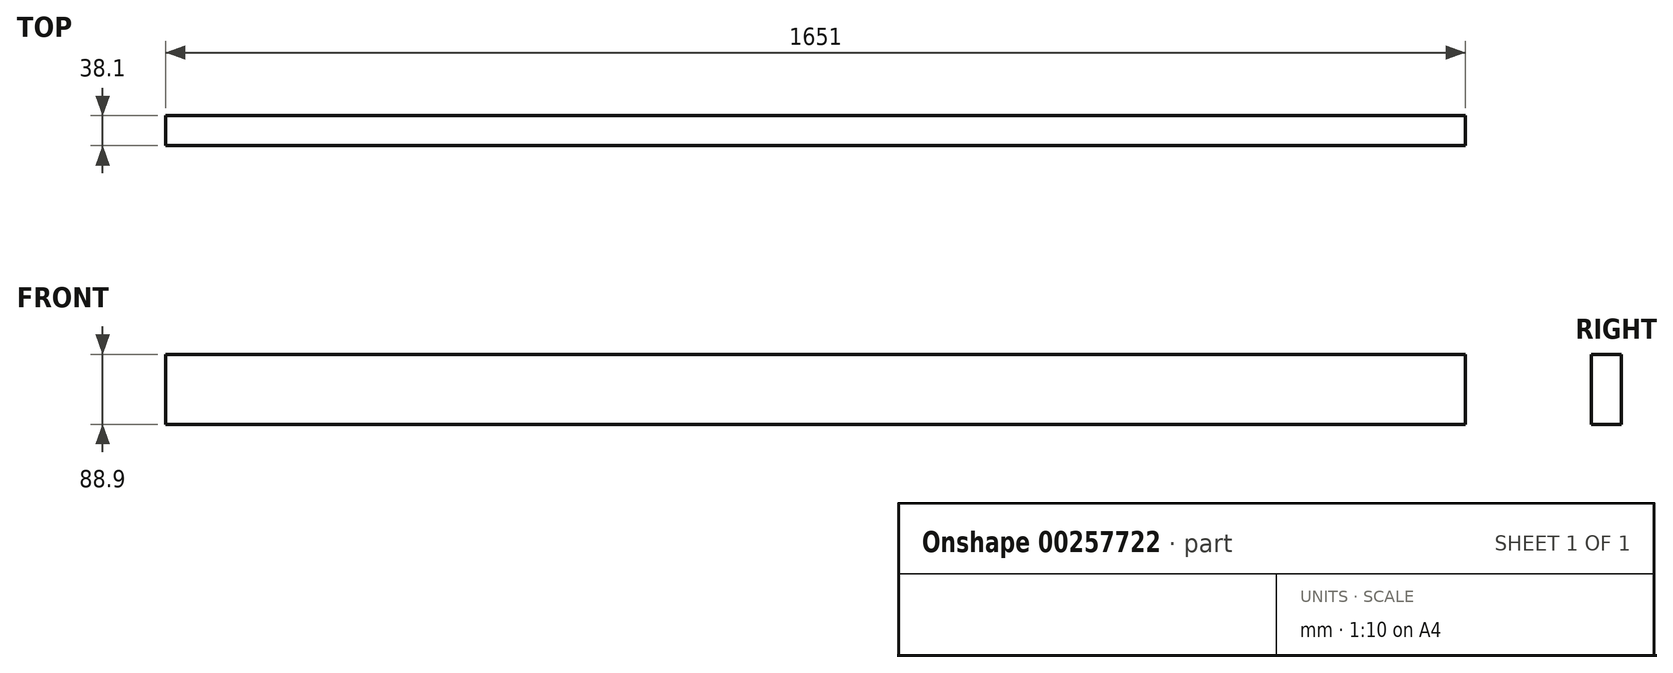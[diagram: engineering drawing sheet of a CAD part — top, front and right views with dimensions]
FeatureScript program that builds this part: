
annotation { "Feature Type Name" : "Feature", "Feature Type Description" : "" }
export const myFeature = defineFeature(function(context is Context, id is Id, definition is map)
    precondition{}
    {
        {
            var Q0;
            Q0=qCreatedBy(makeId("Top.planeOp"),FACE);
            var sketch = newSketch(context, id + "F0", { "sketchPlane" : qUnion([Q0])});
            skLineSegment(sketch, "E0.bottom", {"start": v(-825.5, 19.05) * mm, "end": v(825.5, 19.05) * mm});
            skLineSegment(sketch, "E0.top", {"start": v(-825.5, -19.05) * mm, "end": v(825.5, -19.05) * mm});
            skLineSegment(sketch, "E0.left", {"start": v(-825.5, 19.05) * mm, "end": v(-825.5, -19.05) * mm});
            skLineSegment(sketch, "E0.right", {"start": v(825.5, 19.05) * mm, "end": v(825.5, -19.05) * mm});
            skSolve(sketch);
        }
        {
            var Q0;
            Q0=makeQuery(id+"F0.imprint","IMPRINT",FACE,{"disambiguationData":[TD([[makeQuery(id+"F0.imprint","IMPRINT",EDGE,{"derivedFrom":sQuery(id+"F0.wireOp",EDGE,"E0.bottom")}),-1.0]])]});
            extrude(context, id + "F1", {"entities" : qUnion([Q0]), "endBound" : BoundingType.SYMMETRIC, "depth" : 88.9 * mm});
        }
    });
